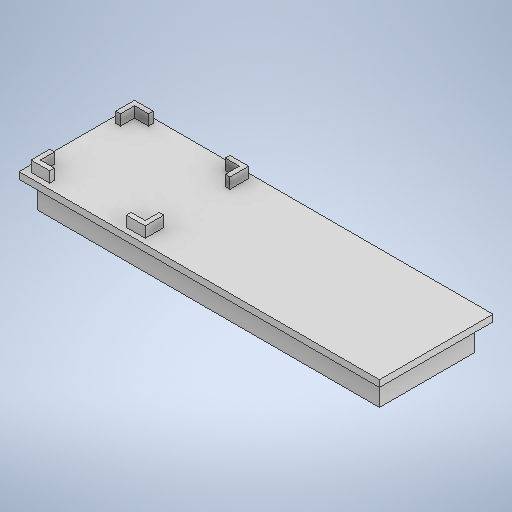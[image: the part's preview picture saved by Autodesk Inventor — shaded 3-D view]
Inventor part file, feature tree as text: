
AUTODESK INVENTOR PART (.ipt)
format: ipt  version: 2025 (Build 290162010, 162A)  size: 449,536 bytes
history: native  units: in
note: dims shown in document units (in); Inventor stores cm internally (conversion verified against a paired STEP export)
features: move_body x12, direct_edit x8, sketch x7, extrude x5, mirror x3
ambient origin geometry x8: Origin, YZ Plane, XZ Plane, XY Plane, X Axis, Y Axis, Z Axis, Center Point
bodies: Solid1 (feature_tree)
feature tree (35):
  extrude  "Extrusion1"  Depth=5.1181in
  sketch  "Sketch2"  dims[d2=0.1378in d3=0.1378in]
  extrude  "Extrusion2"  Depth=0.1378in
  extrude  "Extrusion3"  Depth=0.1378in
  mirror  "Mirror1"
  direct_edit  "Direct Edit1"
  sketch  "Sketch5"  dims[d9=0.0443in d10=0.2953in d11=0.0in]
  sketch  "Sketch6"  dims[d12=1.3386in]
  extrude  "Extrusion4"  Depth=0.0344in
  mirror  "Mirror2"
  extrude  "Extrusion5"  Depth=0.2953in TaperAngle=0.0deg
  mirror  "Mirror3"
  direct_edit  "Direct Edit2"
  direct_edit  "Direct Edit3"
  direct_edit  "Direct Edit4"
  direct_edit  "Direct Edit5"
  direct_edit  "Direct Edit6"
  direct_edit  "Direct Edit7"
  direct_edit  "Direct Edit8"
  sketch  "Sketch1"  dims[d0=1.4764in d1=5.1181in]
  sketch  "Sketch3"  dims[d4=0.1378in d5=0.1378in]
  sketch  "Sketch4"  dims[d6=0.0984in d7=0.0in d8=0.0344in]
  sketch  "Sketch7"  dims[d13=1.4961in d14=1.4764in d15=0.0689in d16=0.0689in d17=0.0689in d18=0.2756in d19=0.2756in d20=0.2756in d21=0.2756in d22=0.1575in d23=0.0in d24=0.0in d25=0.0in d26=0.0984in d27=0.0984in d28=0.0984in d29=0.0in d30=0.0984in d31=0.0in d32=0.0in d33=-0.0394in d34=0.0in d35=0.0in d36=-0.0394in d37=0.0in d38=0.0394in d39=0.0in d40=0.0in d41=0.0394in d42=0.0in d43=0.0in d44=-0.0295in d45=0.0in d46=0.0in d47=0.0in d48=0.0in d49=-0.0098in d50=0.0in d51=0.0197in d52=0.0in d53=0.0in d54=0.0in d55=0.0394in d56=0.0in d57=0.0in d58=0.0394in d59=0.0in d60=0.0in d61=0.0394in d62=0.0in d63=0.0in d64=0.0394in]
  move_body  "Move1"
  move_body  "Move2"
  move_body  "Move3"
  move_body  "Move4"
  move_body  "Move5"
  move_body  "Move6"
  move_body  "Move7"
  move_body  "Move8"
  move_body  "Move9"
  move_body  "Move10"
  move_body  "Move11"
  move_body  "Move12"
